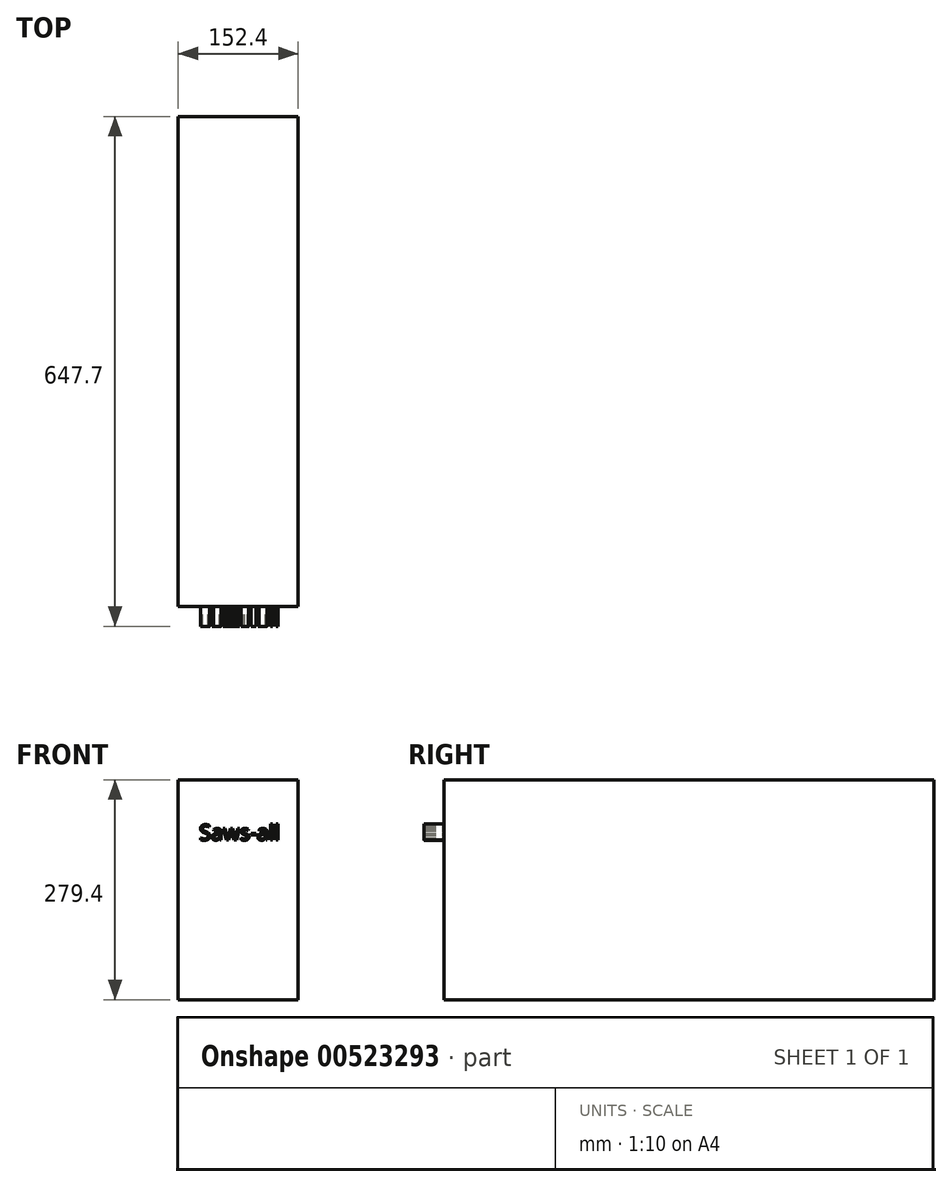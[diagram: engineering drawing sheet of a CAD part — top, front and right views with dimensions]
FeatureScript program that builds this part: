
annotation { "Feature Type Name" : "Feature", "Feature Type Description" : "" }
export const myFeature = defineFeature(function(context is Context, id is Id, definition is map)
    precondition{}
    {
        {
            var Q0;
            Q0=qCreatedBy(makeId("Front.planeOp"),FACE);
            var sketch = newSketch(context, id + "F0", { "sketchPlane" : qUnion([Q0])});
            skLineSegment(sketch, "E0.bottom", {"start": v(76.2, 139.7) * mm, "end": v(-76.2, 139.7) * mm});
            skLineSegment(sketch, "E0.top", {"start": v(76.2, -139.7) * mm, "end": v(-76.2, -139.7) * mm});
            skLineSegment(sketch, "E0.left", {"start": v(76.2, 139.7) * mm, "end": v(76.2, -139.7) * mm});
            skLineSegment(sketch, "E0.right", {"start": v(-76.2, 139.7) * mm, "end": v(-76.2, -139.7) * mm});
            skPoint(sketch, "E0.middle", {"position": v(0, 0) * mm});
            skSolve(sketch);
        }
        {
            var Q0;
            Q0=makeQuery(id+"F0.imprint","IMPRINT",FACE,{"disambiguationData":[TD([[makeQuery(id+"F0.imprint","IMPRINT",EDGE,{"derivedFrom":sQuery(id+"F0.wireOp",EDGE,"E0.bottom")}),1.0]])]});
            extrude(context, id + "F1", {"entities" : qUnion([Q0]), "depth" : 622.3 * mm, "offsetDistance" : 25.4 * mm});
        }
        {
            var Q0;
            Q0=makeQuery(id+"F1.opExtrude","CAP_FACE",FACE,{"disambiguationData":[OSD([sQuery(id+"F0.wireOp",EDGE,"E0.bottom"),sQuery(id+"F0.wireOp",EDGE,"E0.top"),sQuery(id+"F0.wireOp",EDGE,"E0.left"),sQuery(id+"F0.wireOp",EDGE,"E0.right")])],"isStart":false});
            var sketch = newSketch(context, id + "F2", { "sketchPlane" : qUnion([Q0])});
            skText(sketch, "E1", { "text": "Saws-all", "fontName": "OpenSans-Regular.ttf"});
            const initialGuessF2  = {"E1": [-0.04943, 0.063, 1, 0, 0.01965]};
            skSetInitialGuess(sketch, initialGuessF2);
            skSolve(sketch);
        }
        {
            var Q0;
            Q0 = qSketchRegion(id + "F2", true);
            extrude(context, id + "F3", {"entities" : qUnion([Q0]), "operationType" : NewBodyOperationType.ADD, "depth" : 25.4 * mm, "offsetDistance" : 25.4 * mm});
        }
    });
